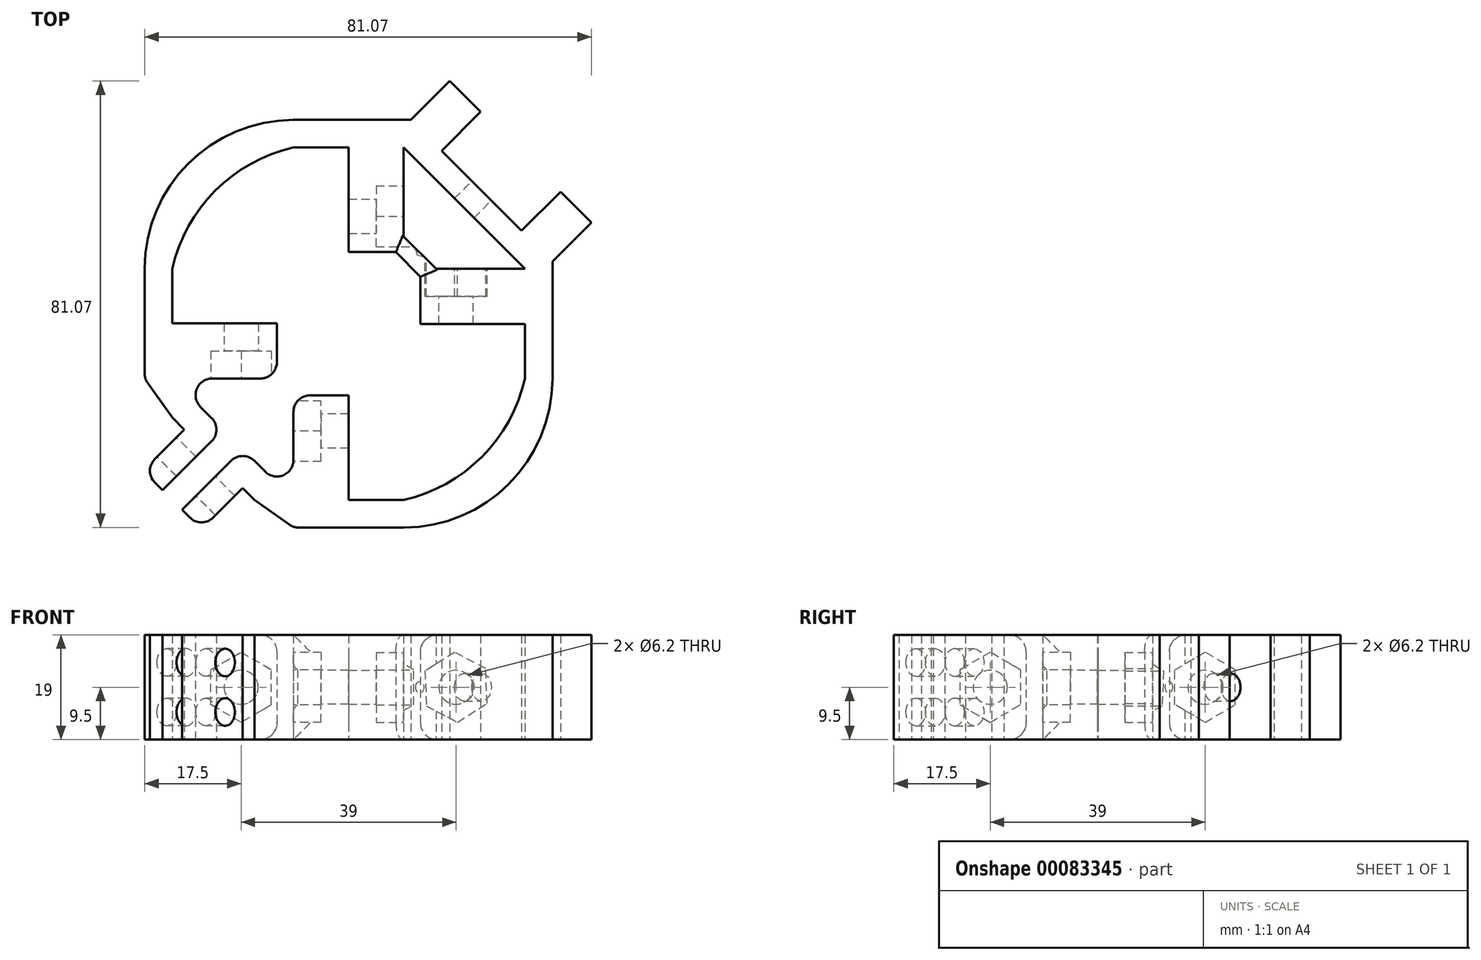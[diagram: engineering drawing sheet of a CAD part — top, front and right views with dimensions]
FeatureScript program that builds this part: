
annotation { "Feature Type Name" : "Feature", "Feature Type Description" : "" }
export const myFeature = defineFeature(function(context is Context, id is Id, definition is map)
    precondition{}
    {
        {
            var Q0;
            Q0=qCreatedBy(makeId("Top.planeOp"),FACE);
            var sketch = newSketch(context, id + "F0", { "sketchPlane" : qUnion([Q0])});
            skLineSegment(sketch, "E0.bottom", {"start": v(-10, 10) * mm, "end": v(10, 10) * mm, "construction": true});
            skLineSegment(sketch, "E0.top", {"start": v(-10, -10) * mm, "end": v(10, -10) * mm, "construction": true});
            skLineSegment(sketch, "E0.left", {"start": v(-10, 10) * mm, "end": v(-10, -10) * mm, "construction": true});
            skLineSegment(sketch, "E0.right", {"start": v(10, 10) * mm, "end": v(10, -10) * mm, "construction": true});
            skPoint(sketch, "E0.middle", {"position": v(0, 0) * mm});
            skLineSegment(sketch, "E1.0", {"start": v(-19.5, 19.5) * mm, "end": v(19.5, 19.5) * mm, "construction": true});
            skLineSegment(sketch, "E1.1", {"start": v(-19.5, 19.5) * mm, "end": v(-19.5, -19.5) * mm, "construction": true});
            skLineSegment(sketch, "E1.2", {"start": v(-19.5, -19.5) * mm, "end": v(19.5, -19.5) * mm, "construction": true});
            skLineSegment(sketch, "E1.3", {"start": v(19.5, 19.5) * mm, "end": v(19.5, -19.5) * mm, "construction": true});
            skLineSegment(sketch, "E2.0", {"start": v(-29, 29) * mm, "end": v(29, 29) * mm, "construction": true});
            skLineSegment(sketch, "E2.1", {"start": v(-29, 29) * mm, "end": v(-29, -29) * mm, "construction": true});
            skLineSegment(sketch, "E2.2", {"start": v(-29, -29) * mm, "end": v(29, -29) * mm, "construction": true});
            skLineSegment(sketch, "E2.3", {"start": v(29, 29) * mm, "end": v(29, -29) * mm, "construction": true});
            skLineSegment(sketch, "E3", {"start": v(0, 10) * mm, "end": v(0, 29) * mm});
            skLineSegment(sketch, "E4", {"start": v(10, 0) * mm, "end": v(29, 0) * mm, "construction": true});
            skLineSegment(sketch, "E5", {"start": v(0, -10) * mm, "end": v(0, -29) * mm, "construction": true});
            skLineSegment(sketch, "E6", {"start": v(-10, 0) * mm, "end": v(-29, 0) * mm, "construction": true});
            skLineSegment(sketch, "E7.0", {"start": v(-10, 3) * mm, "end": v(-29, 3) * mm, "construction": true});
            skLineSegment(sketch, "E8.0", {"start": v(10, -3) * mm, "end": v(29, -3) * mm, "construction": true});
            skLineSegment(sketch, "E9.0", {"start": v(-10, -3) * mm, "end": v(-29, -3) * mm, "construction": true});
            skLineSegment(sketch, "E10.0", {"start": v(10, 3) * mm, "end": v(29, 3) * mm, "construction": true});
            skLineSegment(sketch, "E11.0", {"start": v(3, 10) * mm, "end": v(3, 29) * mm, "construction": true});
            skLineSegment(sketch, "E12.0", {"start": v(-3, 10) * mm, "end": v(-3, 29) * mm, "construction": true});
            skLineSegment(sketch, "E13.0", {"start": v(-3, -10) * mm, "end": v(-3, -29) * mm, "construction": true});
            skLineSegment(sketch, "E14.0", {"start": v(3, -10) * mm, "end": v(3, -29) * mm, "construction": true});
            skLineSegment(sketch, "E15.0", {"start": v(-32, 32) * mm, "end": v(-32, -32) * mm});
            skLineSegment(sketch, "E15.1", {"start": v(-32, 32) * mm, "end": v(32, 32) * mm});
            skLineSegment(sketch, "E15.2", {"start": v(32, 32) * mm, "end": v(32, -32) * mm});
            skLineSegment(sketch, "E15.3", {"start": v(-32, -32) * mm, "end": v(32, -32) * mm});
            skLineSegment(sketch, "E16.0", {"start": v(-37, 37) * mm, "end": v(37, 37) * mm});
            skLineSegment(sketch, "E16.1", {"start": v(-37, 37) * mm, "end": v(-37, -37) * mm});
            skLineSegment(sketch, "E16.2", {"start": v(-37, -37) * mm, "end": v(37, -37) * mm});
            skLineSegment(sketch, "E16.3", {"start": v(37, 37) * mm, "end": v(37, -37) * mm});
            skLineSegment(sketch, "E17.MirrorCS", {"start": v(0, 13) * mm, "end": v(-10, 13) * mm, "construction": true});
            skLineSegment(sketch, "E18.MirrorCS", {"start": v(-10, 13) * mm, "end": v(-10, 32) * mm, "construction": true});
            skLineSegment(sketch, "E19.MirrorCS", {"start": v(0, 32) * mm, "end": v(0, 13) * mm, "construction": true});
            skLineSegment(sketch, "E20.MirrorCS", {"start": v(10, -13) * mm, "end": v(10, -32) * mm});
            skLineSegment(sketch, "E21.MirrorCS", {"start": v(0, -32) * mm, "end": v(0, -13) * mm});
            skLineSegment(sketch, "E22.MirrorCS", {"start": v(0, -13) * mm, "end": v(10, -13) * mm});
            skLineSegment(sketch, "E23.MirrorCS", {"start": v(32, 0.05) * mm, "end": v(13.05, 0.05) * mm, "construction": true});
            skLineSegment(sketch, "E24.MirrorCS", {"start": v(13.05, -9.95) * mm, "end": v(32, -9.95) * mm, "construction": true});
            skLineSegment(sketch, "E25.MirrorCS", {"start": v(13.05, 0.05) * mm, "end": v(13.05, -9.95) * mm, "construction": true});
            skLineSegment(sketch, "E26.MirrorCS", {"start": v(-32, -0.05) * mm, "end": v(-13, -0.05) * mm});
            skLineSegment(sketch, "E27.MirrorCS", {"start": v(-13, 9.95) * mm, "end": v(-32, 9.95) * mm});
            skLineSegment(sketch, "E28.MirrorCS", {"start": v(-13, -0.05) * mm, "end": v(-13, 9.95) * mm});
            skLineSegment(sketch, "E29", {"start": v(16.28, 32) * mm, "end": v(32, 16.28) * mm});
            skLineSegment(sketch, "E30", {"start": v(16.28, 32) * mm, "end": v(11.28, 37) * mm});
            skLineSegment(sketch, "E31", {"start": v(32, 16.28) * mm, "end": v(37, 11.28) * mm});
            skLineSegment(sketch, "E32", {"start": v(10, 32) * mm, "end": v(32, 9.95) * mm});
            skArc(sketch, "E33", {"start": v(-10, 32) * mm, "mid": v(-25.56, 25.56) * mm, "end": v(-32, 10) * mm});
            skArc(sketch, "E34", {"start": v(-10, 37) * mm, "mid": v(-29.1, 29.1) * mm, "end": v(-37, 10) * mm});
            skArc(sketch, "E35", {"start": v(10, -32) * mm, "mid": v(25.56, -25.56) * mm, "end": v(32, -10) * mm});
            skArc(sketch, "E36", {"start": v(10, -37) * mm, "mid": v(29.1, -29.1) * mm, "end": v(37, -10) * mm});
            skLineSegment(sketch, "E37.MirrorCS", {"start": v(13.05, -0.05) * mm, "end": v(13.05, 9.95) * mm});
            skLineSegment(sketch, "E38.MirrorCS", {"start": v(32, -0.05) * mm, "end": v(13.05, -0.05) * mm});
            skLineSegment(sketch, "E39.MirrorCS", {"start": v(13.05, 9.95) * mm, "end": v(32, 9.95) * mm});
            skLineSegment(sketch, "E40.MirrorCS", {"start": v(-10, -13) * mm, "end": v(-10, -32) * mm});
            skLineSegment(sketch, "E41.MirrorCS", {"start": v(0, -13) * mm, "end": v(-10, -13) * mm});
            skLineSegment(sketch, "E42.MirrorCS", {"start": v(-13, -9.95) * mm, "end": v(-32, -9.95) * mm});
            skLineSegment(sketch, "E43.MirrorCS", {"start": v(-32, 0.05) * mm, "end": v(-13, 0.05) * mm});
            skLineSegment(sketch, "E44.MirrorCS", {"start": v(-13, 0.05) * mm, "end": v(-13, -9.95) * mm});
            skLineSegment(sketch, "E45.MirrorCS", {"start": v(0, 13) * mm, "end": v(10, 13) * mm});
            skLineSegment(sketch, "E46.MirrorCS", {"start": v(0, 32) * mm, "end": v(0, 13) * mm});
            skLineSegment(sketch, "E47.MirrorCS", {"start": v(10, 13) * mm, "end": v(10, 32) * mm});
            skLineSegment(sketch, "E48", {"start": v(10, 13) * mm, "end": v(13.05, 9.95) * mm});
            skLineSegment(sketch, "E49", {"start": v(-32, -9.95) * mm, "end": v(-37, -10) * mm});
            skLineSegment(sketch, "E50", {"start": v(-10, -32) * mm, "end": v(-10, -37) * mm});
            skLineSegment(sketch, "E51", {"start": v(10, 15.83) * mm, "end": v(15.88, 9.95) * mm});
            skLineSegment(sketch, "E52", {"start": v(8.59, 13) * mm, "end": v(13.05, 8.54) * mm});
            skLineSegment(sketch, "E53", {"start": v(-32, -9.95) * mm, "end": v(-10, -32) * mm});
            skLineSegment(sketch, "E54.0", {"start": v(-35.54, -13.48) * mm, "end": v(-13.54, -35.53) * mm, "construction": true});
            skLineSegment(sketch, "E55", {"start": v(-32, -17.03) * mm, "end": v(-17.06, -32) * mm});
            skLineSegment(sketch, "E56", {"start": v(-32, -32) * mm, "end": v(-20.98, -21) * mm, "construction": true});
            skLineSegment(sketch, "E57.0", {"start": v(-30.94, -33.06) * mm, "end": v(-19.92, -22.06) * mm, "construction": true});
            skLineSegment(sketch, "E58.0", {"start": v(-33.06, -30.94) * mm, "end": v(-22.04, -19.94) * mm, "construction": true});
            skLineSegment(sketch, "E59", {"start": v(-22.04, -19.94) * mm, "end": v(-25.57, -23.47) * mm});
            skLineSegment(sketch, "E60", {"start": v(-23.46, -25.6) * mm, "end": v(-19.92, -22.06) * mm});
            skLineSegment(sketch, "E61", {"start": v(-25.57, -23.47) * mm, "end": v(-29, -26.89) * mm});
            skLineSegment(sketch, "E62", {"start": v(-29, -26.89) * mm, "end": v(-33.24, -22.64) * mm});
            skLineSegment(sketch, "E63", {"start": v(-33.24, -22.64) * mm, "end": v(-29.81, -19.22) * mm});
            skLineSegment(sketch, "E64", {"start": v(-23.46, -25.6) * mm, "end": v(-26.87, -29) * mm});
            skLineSegment(sketch, "E65", {"start": v(-26.87, -29) * mm, "end": v(-22.63, -33.25) * mm});
            skLineSegment(sketch, "E66", {"start": v(-22.63, -33.25) * mm, "end": v(-19.22, -29.84) * mm});
            skLineSegment(sketch, "E67", {"start": v(-32, -17.03) * mm, "end": v(-37, -10) * mm});
            skLineSegment(sketch, "E68", {"start": v(-17.06, -32) * mm, "end": v(-10, -37) * mm});
            skLineSegment(sketch, "E69", {"start": v(-26.87, -29) * mm, "end": v(-30.94, -33.06) * mm});
            skLineSegment(sketch, "E70", {"start": v(-30.94, -33.06) * mm, "end": v(-26.7, -37.3) * mm});
            skLineSegment(sketch, "E71", {"start": v(-26.7, -37.3) * mm, "end": v(-22.63, -33.25) * mm});
            skLineSegment(sketch, "E72", {"start": v(-29, -26.89) * mm, "end": v(-33.06, -30.94) * mm});
            skLineSegment(sketch, "E73", {"start": v(-33.06, -30.94) * mm, "end": v(-37.3, -26.7) * mm});
            skLineSegment(sketch, "E74", {"start": v(-37.3, -26.7) * mm, "end": v(-33.24, -22.64) * mm});
            skLineSegment(sketch, "E75.0", {"start": v(-29.7, -26.18) * mm, "end": v(-33.77, -30.23) * mm});
            skLineSegment(sketch, "E75.1", {"start": v(-26.28, -22.76) * mm, "end": v(-29.7, -26.18) * mm});
            skLineSegment(sketch, "E75.2", {"start": v(-22.74, -19.23) * mm, "end": v(-26.28, -22.76) * mm});
            skLineSegment(sketch, "E76.0", {"start": v(-22.75, -26.3) * mm, "end": v(-19.2, -22.77) * mm});
            skLineSegment(sketch, "E76.1", {"start": v(-22.75, -26.3) * mm, "end": v(-26.16, -29.7) * mm});
            skLineSegment(sketch, "E76.2", {"start": v(-26.16, -29.7) * mm, "end": v(-30.23, -33.77) * mm});
            skArc(sketch, "E77", {"start": v(-10, 32) * mm, "mid": v(-24.18, 24.18) * mm, "end": v(-32, 10) * mm});
            skArc(sketch, "E78", {"start": v(10, -32) * mm, "mid": v(24.19, -24.16) * mm, "end": v(32, -9.95) * mm});
            skSolve(sketch);
        }
        {
            var Q0;
            {var subQ0=sQuery(id+"F0.wireOp",EDGE,"E29");Q0=makeQuery(id+"F0.imprint","IMPRINT",FACE,{"disambiguationData":[TD([[makeQuery(id+"F0.imprint","IMPRINT",EDGE,{"derivedFrom":subQ0}),-1.0]])]});}
            var Q1;
            {var subQ0=sQuery(id+"F0.wireOp",EDGE,"E30");Q1=makeQuery(id+"F0.imprint","IMPRINT",FACE,{"disambiguationData":[TD([[makeQuery(id+"F0.imprint","IMPRINT",EDGE,{"derivedFrom":subQ0}),1.0]])]});}
            var Q2;
            {var subQ6=sQuery(id+"F0.wireOp",EDGE,"E31");Q2=makeQuery(id+"F0.imprint","IMPRINT",FACE,{"disambiguationData":[TD([[makeQuery(id+"F0.imprint","IMPRINT",EDGE,{"derivedFrom":subQ6}),-1.0]])]});}
            var Q3;
            Q3=makeQuery(id+"F0.imprint","IMPRINT",FACE,{"disambiguationData":[TD([[makeQuery(id+"F0.imprint","IMPRINT",EDGE,{"derivedFrom":sQuery(id+"F0.wireOp",EDGE,"E37.MirrorCS")}),-1.0]])]});
            var Q4;
            Q4=makeQuery(id+"F0.imprint","IMPRINT",FACE,{"disambiguationData":[TD([[makeQuery(id+"F0.imprint","IMPRINT",EDGE,{"derivedFrom":sQuery(id+"F0.wireOp",EDGE,"E45.MirrorCS")}),1.0]])]});
            var Q5;
            {var subQ0=sQuery(id+"F0.wireOp",EDGE,"E26.MirrorCS");Q5=makeQuery(id+"F0.imprint","IMPRINT",FACE,{"disambiguationData":[TD([[makeQuery(id+"F0.imprint","IMPRINT",EDGE,{"derivedFrom":subQ0}),1.0]])]});}
            var Q6;
            {var subQ8=sQuery(id+"F0.wireOp",EDGE,"E50");Q6=makeQuery(id+"F0.imprint","IMPRINT",FACE,{"disambiguationData":[TD([[makeQuery(id+"F0.imprint","IMPRINT",EDGE,{"derivedFrom":subQ8}),1.0]])]});}
            var Q7;
            {var subQ0=sQuery(id+"F0.wireOp",EDGE,"E35");Q7=makeQuery(id+"F0.imprint","IMPRINT",FACE,{"disambiguationData":[TD([[makeQuery(id+"F0.imprint","IMPRINT",EDGE,{"derivedFrom":subQ0}),-1.0]])]});}
            var Q8;
            {var subQ0=sQuery(id+"F0.wireOp",EDGE,"E49");Q8=makeQuery(id+"F0.imprint","IMPRINT",FACE,{"disambiguationData":[TD([[makeQuery(id+"F0.imprint","IMPRINT",EDGE,{"derivedFrom":subQ0}),-1.0]])]});}
            var Q9;
            {var subQ0=sQuery(id+"F0.wireOp",EDGE,"E33");Q9=makeQuery(id+"F0.imprint","IMPRINT",FACE,{"disambiguationData":[TD([[makeQuery(id+"F0.imprint","IMPRINT",EDGE,{"derivedFrom":subQ0}),-1.0]])]});}
            var Q10;
            {var subQ0=sQuery(id+"F0.wireOp",EDGE,"E48");Q10=makeQuery(id+"F0.imprint","IMPRINT",FACE,{"disambiguationData":[TD([[makeQuery(id+"F0.imprint","IMPRINT",EDGE,{"derivedFrom":subQ0}),1.0]])]});}
            var Q11;
            {var subQ0=sQuery(id+"F0.wireOp",EDGE,"E48");Q11=makeQuery(id+"F0.imprint","IMPRINT",FACE,{"disambiguationData":[TD([[makeQuery(id+"F0.imprint","IMPRINT",EDGE,{"derivedFrom":subQ0}),-1.0]])]});}
            var Q12;
            {var subQ0=sQuery(id+"F0.wireOp",EDGE,"E49");Q12=makeQuery(id+"F0.imprint","IMPRINT",FACE,{"disambiguationData":[TD([[makeQuery(id+"F0.imprint","IMPRINT",EDGE,{"derivedFrom":subQ0}),1.0]])]});}
            var Q13;
            {var subQ0=sQuery(id+"F0.wireOp",EDGE,"E50");Q13=makeQuery(id+"F0.imprint","IMPRINT",FACE,{"disambiguationData":[TD([[makeQuery(id+"F0.imprint","IMPRINT",EDGE,{"derivedFrom":subQ0}),-1.0]])]});}
            var Q14;
            {var subQ0=sQuery(id+"F0.wireOp",EDGE,"E62");var subQ1=sQuery(id+"F0.wireOp",EDGE,"E15.0");var subQ2=makeQuery(id+"F0.imprint","INTERSECT",VERTEX,{"derivedFrom":[subQ1,subQ0]});Q14=makeQuery(id+"F0.imprint","IMPRINT",FACE,{"disambiguationData":[TD([[makeQuery(id+"F0.imprint","IMPRINT",EDGE,{"disambiguationData":[TD([[subQ2,-1.0]])],"derivedFrom":subQ1}),1.0]])]});}
            var Q15;
            {var subQ0=sQuery(id+"F0.wireOp",EDGE,"E73");Q15=makeQuery(id+"F0.imprint","IMPRINT",FACE,{"disambiguationData":[TD([[makeQuery(id+"F0.imprint","IMPRINT",EDGE,{"derivedFrom":subQ0}),-1.0]])]});}
            var Q16;
            {var subQ0=sQuery(id+"F0.wireOp",EDGE,"E70");Q16=makeQuery(id+"F0.imprint","IMPRINT",FACE,{"disambiguationData":[TD([[makeQuery(id+"F0.imprint","IMPRINT",EDGE,{"derivedFrom":subQ0}),1.0]])]});}
            var Q17;
            {var subQ0=sQuery(id+"F0.wireOp",EDGE,"E65");var subQ1=sQuery(id+"F0.wireOp",EDGE,"E15.3");var subQ2=makeQuery(id+"F0.imprint","INTERSECT",VERTEX,{"derivedFrom":[subQ1,subQ0]});Q17=makeQuery(id+"F0.imprint","IMPRINT",FACE,{"disambiguationData":[TD([[makeQuery(id+"F0.imprint","IMPRINT",EDGE,{"disambiguationData":[TD([[subQ2,-1.0]])],"derivedFrom":subQ1}),-1.0]])]});}
            var Q18;
            {var subQ0=sQuery(id+"F0.wireOp",EDGE,"E63");var subQ1=sQuery(id+"F0.wireOp",EDGE,"E15.0");var subQ2=makeQuery(id+"F0.imprint","INTERSECT",VERTEX,{"derivedFrom":[subQ1,subQ0]});Q18=makeQuery(id+"F0.imprint","IMPRINT",FACE,{"disambiguationData":[TD([[makeQuery(id+"F0.imprint","IMPRINT",EDGE,{"disambiguationData":[TD([[subQ2,-1.0]])],"derivedFrom":subQ1}),-1.0]])]});}
            var Q19;
            {var subQ0=sQuery(id+"F0.wireOp",EDGE,"E21.MirrorCS");Q19=makeQuery(id+"F0.imprint","IMPRINT",FACE,{"disambiguationData":[TD([[makeQuery(id+"F0.imprint","IMPRINT",EDGE,{"derivedFrom":subQ0}),1.0]])]});}
            var Q20;
            {var subQ0=sQuery(id+"F0.wireOp",EDGE,"E26.MirrorCS");Q20=makeQuery(id+"F0.imprint","IMPRINT",FACE,{"disambiguationData":[TD([[makeQuery(id+"F0.imprint","IMPRINT",EDGE,{"derivedFrom":subQ0}),-1.0]])]});}
            var Q21;
            {var subQ3=sQuery(id+"F0.wireOp",EDGE,"E15.0");var subQ6=sQuery(id+"F0.wireOp",EDGE,"E62");var subQ10=makeQuery(id+"F0.imprint","INTERSECT",VERTEX,{"derivedFrom":[subQ3,subQ6]});Q21=makeQuery(id+"F0.imprint","IMPRINT",FACE,{"disambiguationData":[TD([[makeQuery(id+"F0.imprint","IMPRINT",EDGE,{"disambiguationData":[TD([[subQ10,-1.0]])],"derivedFrom":subQ3}),-1.0]])]});}
            var Q22;
            {var subQ6=sQuery(id+"F0.wireOp",EDGE,"E75.2");Q22=makeQuery(id+"F0.imprint","IMPRINT",FACE,{"disambiguationData":[TD([[makeQuery(id+"F0.imprint","IMPRINT",EDGE,{"derivedFrom":subQ6}),-1.0]])]});}
            var Q23;
            {var subQ5=sQuery(id+"F0.wireOp",EDGE,"E75.1");Q23=makeQuery(id+"F0.imprint","IMPRINT",FACE,{"disambiguationData":[TD([[makeQuery(id+"F0.imprint","IMPRINT",EDGE,{"derivedFrom":subQ5}),-1.0]])]});}
            var Q24;
            {var subQ6=sQuery(id+"F0.wireOp",EDGE,"E76.0");Q24=makeQuery(id+"F0.imprint","IMPRINT",FACE,{"disambiguationData":[TD([[makeQuery(id+"F0.imprint","IMPRINT",EDGE,{"derivedFrom":subQ6}),-1.0]])]});}
            var Q25;
            {var subQ0=sQuery(id+"F0.wireOp",EDGE,"E76.1");Q25=makeQuery(id+"F0.imprint","IMPRINT",FACE,{"disambiguationData":[TD([[makeQuery(id+"F0.imprint","IMPRINT",EDGE,{"derivedFrom":subQ0}),1.0]])]});}
            var Q26;
            {var subQ0=sQuery(id+"F0.wireOp",EDGE,"E76.2");var subQ8=sQuery(id+"F0.wireOp",EDGE,"E15.3");var subQ11=makeQuery(id+"F0.imprint","INTERSECT",VERTEX,{"derivedFrom":[subQ8,subQ0]});Q26=makeQuery(id+"F0.imprint","IMPRINT",FACE,{"disambiguationData":[TD([[makeQuery(id+"F0.imprint","IMPRINT",EDGE,{"disambiguationData":[TD([[subQ11,-1.0]])],"derivedFrom":subQ8}),-1.0]])]});}
            var Q27;
            {var subQ0=sQuery(id+"F0.wireOp",EDGE,"E76.2");var subQ1=sQuery(id+"F0.wireOp",EDGE,"E15.3");var subQ2=makeQuery(id+"F0.imprint","INTERSECT",VERTEX,{"derivedFrom":[subQ1,subQ0]});Q27=makeQuery(id+"F0.imprint","IMPRINT",FACE,{"disambiguationData":[TD([[makeQuery(id+"F0.imprint","IMPRINT",EDGE,{"disambiguationData":[TD([[subQ2,-1.0]])],"derivedFrom":subQ1}),1.0]])]});}
            var Q28;
            Q28=makeQuery(id+"F0.imprint","IMPRINT",FACE,{"disambiguationData":[TD([[makeQuery(id+"F0.imprint","IMPRINT",EDGE,{"derivedFrom":sQuery(id+"F0.wireOp",EDGE,"E33")}),1.0]])]});
            var Q29;
            {var subQ0=sQuery(id+"F0.wireOp",EDGE,"E35");Q29=makeQuery(id+"F0.imprint","IMPRINT",FACE,{"disambiguationData":[TD([[makeQuery(id+"F0.imprint","IMPRINT",EDGE,{"derivedFrom":subQ0}),1.0]])]});}
            extrude(context, id + "F1", {"entities" : qUnion([Q0, Q1, Q2, Q3, Q4, Q5, Q6, Q7, Q8, Q9, Q10, Q11, Q12, Q13, Q14, Q15, Q16, Q17, Q18, Q19, Q20, Q21, Q22, Q23, Q24, Q25, Q26, Q27, Q28, Q29]), "depth" : 19 * mm});
        }
        {
            var Q0;
            Q0=makeQuery(id+"F1.opExtrude","SWEPT_FACE",FACE,{"disambiguationData":[OSD([sQuery(id+"F0.wireOp",EDGE,"E40.MirrorCS")])]});
            var sketch = newSketch(context, id + "F2", { "sketchPlane" : qUnion([Q0])});
            skLineSegment(sketch, "E79", {"start": v(19.5, 9.5) * mm, "end": v(32, 9.5) * mm, "construction": true});
            skCircle(sketch, "E80.cCircle", {"center": v(19.5, 9.5) * mm, "radius": 5.5 * mm, "construction": true});
            skLineSegment(sketch, "E80.0", {"start": v(14, 6.32) * mm, "end": v(14, 12.68) * mm});
            skLineSegment(sketch, "E80.1", {"start": v(14, 12.68) * mm, "end": v(19.5, 15.85) * mm});
            skLineSegment(sketch, "E80.2", {"start": v(19.5, 15.85) * mm, "end": v(25, 12.68) * mm});
            skLineSegment(sketch, "E80.3", {"start": v(25, 12.68) * mm, "end": v(25, 6.32) * mm});
            skLineSegment(sketch, "E80.4", {"start": v(25, 6.32) * mm, "end": v(19.5, 3.15) * mm});
            skLineSegment(sketch, "E80.5", {"start": v(19.5, 3.15) * mm, "end": v(14, 6.32) * mm});
            skPoint(sketch, "E80.0.midPoint", {"position": v(14, 9.5) * mm});
            skSolve(sketch);
        }
        {
            var Q0;
            Q0=makeQuery(id+"F2.imprint","IMPRINT",FACE,{"disambiguationData":[TD([[makeQuery(id+"F2.imprint","IMPRINT",EDGE,{"derivedFrom":sQuery(id+"F2.wireOp",EDGE,"b893e4e9-6a1b-4cab-829b-d1a7efe0a6880.MirrorCS")}),1.0]])]});
            var Q1;
            Q1=makeQuery(id+"F2.imprint","IMPRINT",FACE,{"disambiguationData":[TD([[makeQuery(id+"F2.imprint","IMPRINT",EDGE,{"derivedFrom":sQuery(id+"F2.wireOp",EDGE,"E80.0")}),-1.0]])]});
            extrude(context, id + "F3", {"entities" : qUnion([Q0, Q1]), "operationType" : NewBodyOperationType.REMOVE, "oppositeDirection" : true, "depth" : 5 * mm});
        }
        {
            var Q0;
            Q0=makeQuery(id+"F1.opExtrude","SWEPT_FACE",FACE,{"disambiguationData":[OSD([sQuery(id+"F0.wireOp",EDGE,"E42.MirrorCS")])]});
            var sketch = newSketch(context, id + "F4", { "sketchPlane" : qUnion([Q0])});
            skLineSegment(sketch, "E81", {"start": v(-32, 9.5) * mm, "end": v(-19.5, 9.5) * mm, "construction": true});
            skPoint(sketch, "E81.endSnap0", {"position": v(-32, 9.5) * mm});
            skCircle(sketch, "E82.cCircle", {"center": v(-19.5, 9.5) * mm, "radius": 5.5 * mm, "construction": true});
            skLineSegment(sketch, "E82.0", {"start": v(-14, 12.68) * mm, "end": v(-14, 6.32) * mm});
            skLineSegment(sketch, "E82.1", {"start": v(-14, 6.32) * mm, "end": v(-19.5, 3.15) * mm});
            skLineSegment(sketch, "E82.2", {"start": v(-19.5, 3.15) * mm, "end": v(-25, 6.32) * mm});
            skLineSegment(sketch, "E82.3", {"start": v(-25, 6.32) * mm, "end": v(-25, 12.68) * mm});
            skLineSegment(sketch, "E82.4", {"start": v(-25, 12.68) * mm, "end": v(-19.5, 15.85) * mm});
            skLineSegment(sketch, "E82.5", {"start": v(-19.5, 15.85) * mm, "end": v(-14, 12.68) * mm});
            skPoint(sketch, "E82.0.midPoint", {"position": v(-14, 9.5) * mm});
            skSolve(sketch);
        }
        {
            var Q0;
            Q0=makeQuery(id+"F4.imprint","IMPRINT",FACE,{"disambiguationData":[TD([[makeQuery(id+"F4.imprint","IMPRINT",EDGE,{"derivedFrom":sQuery(id+"F4.wireOp",EDGE,"E82.0")}),-1.0]])]});
            extrude(context, id + "F5", {"entities" : qUnion([Q0]), "operationType" : NewBodyOperationType.REMOVE, "oppositeDirection" : true, "depth" : 5 * mm});
        }
        {
            var Q0;
            Q0=makeQuery(id+"F1.opExtrude","SWEPT_FACE",FACE,{"disambiguationData":[OSD([sQuery(id+"F0.wireOp",EDGE,"E47.MirrorCS")])]});
            var sketch = newSketch(context, id + "F6", { "sketchPlane" : qUnion([Q0])});
            skSolve(sketch);
        }
        {
            var Q0;
            Q0=makeQuery(id+"F1.opExtrude","SWEPT_FACE",FACE,{"disambiguationData":[OSD([sQuery(id+"F0.wireOp",EDGE,"E39.MirrorCS")])]});
            var sketch = newSketch(context, id + "F7", { "sketchPlane" : qUnion([Q0])});
            skLineSegment(sketch, "E83", {"start": v(-32, 9.5) * mm, "end": v(-19.5, 9.5) * mm, "construction": true});
            skCircle(sketch, "E84.cCircle", {"center": v(-19.5, 9.5) * mm, "radius": 5.5 * mm, "construction": true});
            skLineSegment(sketch, "E84.0", {"start": v(-13.87, 12.45) * mm, "end": v(-14.13, 6.1) * mm});
            skLineSegment(sketch, "E84.1", {"start": v(-14.13, 6.1) * mm, "end": v(-19.76, 3.15) * mm});
            skLineSegment(sketch, "E84.2", {"start": v(-19.76, 3.15) * mm, "end": v(-25.13, 6.55) * mm});
            skLineSegment(sketch, "E84.3", {"start": v(-25.13, 6.55) * mm, "end": v(-24.87, 12.9) * mm});
            skLineSegment(sketch, "E84.4", {"start": v(-24.87, 12.9) * mm, "end": v(-19.24, 15.85) * mm});
            skLineSegment(sketch, "E84.5", {"start": v(-19.24, 15.85) * mm, "end": v(-13.87, 12.45) * mm});
            skPoint(sketch, "E84.0.midPoint", {"position": v(-14, 9.27) * mm});
            skSolve(sketch);
        }
        {
            var Q0;
            Q0=makeQuery(id+"F7.imprint","IMPRINT",FACE,{"disambiguationData":[TD([[makeQuery(id+"F7.imprint","IMPRINT",EDGE,{"derivedFrom":sQuery(id+"F7.wireOp",EDGE,"E84.0")}),-1.0]])]});
            var Q1;
            {var subQ1=sQuery(id+"F7.wireOp",EDGE,"E84.2");Q1=makeQuery(id+"F7.imprint","IMPRINT",FACE,{"disambiguationData":[TD([[makeQuery(id+"F7.imprint","IMPRINT",EDGE,{"derivedFrom":subQ1}),-1.0]])]});}
            extrude(context, id + "F8", {"entities" : qUnion([Q0, Q1]), "operationType" : NewBodyOperationType.REMOVE, "endBound" : BoundingType.SYMMETRIC, "oppositeDirection" : true, "depth" : 10 * mm});
        }
        {
            var Q0;
            {var subQ0=sQuery(id+"F0.wireOp",EDGE,"E47.MirrorCS");Q0=makeQuery(id+"F6.imprint","IMPRINT",FACE,{"disambiguationData":[TD([[makeQuery(id+"F6.imprint","IMPRINT",EDGE,{"derivedFrom":makeQuery(id+"F1.opExtrude","CAP_EDGE",EDGE,{"disambiguationData":[OSD([subQ0])],"isStart":true})}),1.0]])]});}
            var sketch = newSketch(context, id + "F9", { "sketchPlane" : qUnion([Q0])});
            skLineSegment(sketch, "E85.0", {"start": v(19.5, 22) * mm, "end": v(19.5, -3) * mm, "construction": true});
            skCircle(sketch, "E86.cCircle", {"center": v(19.5, 9.5) * mm, "radius": 5.5 * mm, "construction": true});
            skLineSegment(sketch, "E86.0", {"start": v(14, 6.32) * mm, "end": v(14, 12.68) * mm});
            skLineSegment(sketch, "E86.1", {"start": v(14, 12.68) * mm, "end": v(19.5, 15.85) * mm});
            skLineSegment(sketch, "E86.2", {"start": v(19.5, 15.85) * mm, "end": v(25, 12.68) * mm});
            skLineSegment(sketch, "E86.3", {"start": v(25, 12.68) * mm, "end": v(25, 6.32) * mm});
            skLineSegment(sketch, "E86.4", {"start": v(25, 6.32) * mm, "end": v(19.5, 3.15) * mm});
            skLineSegment(sketch, "E86.5", {"start": v(19.5, 3.15) * mm, "end": v(14, 6.32) * mm});
            skPoint(sketch, "E86.0.midPoint", {"position": v(14, 9.5) * mm});
            skSolve(sketch);
        }
        {
            var Q0;
            Q0=sQuery(id+"F2.wireOp",VERTEX,"E79.start");
            var Q1;
            Q1=sQuery(id+"F4.wireOp",VERTEX,"E81.end");
            var Q2;
            Q2=sQuery(id+"F9.wireOp",VERTEX,"E86.cCircle.center");
            var Q3;
            Q3=sQuery(id+"F7.wireOp",VERTEX,"E83.end");
            var Q4;
            Q4=makeQuery(id+"F1.opExtrude","SWEPT_BODY",BODY,{"disambiguationData":[OSD([sQuery(id+"F0.wireOp",EDGE,"E15.0"),sQuery(id+"F0.wireOp",EDGE,"E15.1"),sQuery(id+"F0.wireOp",EDGE,"E15.2"),sQuery(id+"F0.wireOp",EDGE,"E15.3"),sQuery(id+"F0.wireOp",EDGE,"E16.0"),sQuery(id+"F0.wireOp",EDGE,"E16.1"),sQuery(id+"F0.wireOp",EDGE,"E16.2"),sQuery(id+"F0.wireOp",EDGE,"E16.3"),sQuery(id+"F0.wireOp",EDGE,"E20.MirrorCS"),sQuery(id+"F0.wireOp",EDGE,"E21.MirrorCS"),sQuery(id+"F0.wireOp",EDGE,"E22.MirrorCS"),sQuery(id+"F0.wireOp",EDGE,"E26.MirrorCS"),sQuery(id+"F0.wireOp",EDGE,"E27.MirrorCS"),sQuery(id+"F0.wireOp",EDGE,"E28.MirrorCS"),sQuery(id+"F0.wireOp",EDGE,"E29"),sQuery(id+"F0.wireOp",EDGE,"E30"),sQuery(id+"F0.wireOp",EDGE,"E31"),sQuery(id+"F0.wireOp",EDGE,"E32"),sQuery(id+"F0.wireOp",EDGE,"E33"),sQuery(id+"F0.wireOp",EDGE,"E34"),sQuery(id+"F0.wireOp",EDGE,"E35"),sQuery(id+"F0.wireOp",EDGE,"E36"),sQuery(id+"F0.wireOp",EDGE,"E37.MirrorCS"),sQuery(id+"F0.wireOp",EDGE,"E38.MirrorCS"),sQuery(id+"F0.wireOp",EDGE,"E39.MirrorCS"),sQuery(id+"F0.wireOp",EDGE,"E45.MirrorCS"),sQuery(id+"F0.wireOp",EDGE,"E46.MirrorCS"),sQuery(id+"F0.wireOp",EDGE,"E47.MirrorCS"),sQuery(id+"F0.wireOp",EDGE,"E49"),sQuery(id+"F0.wireOp",EDGE,"E50")])]});
            hole(context, id + "F10", {"style" : HoleStyle.SIMPLE, "endStyle" : HoleEndStyle.BLIND, "holeDiameter" : 6.2 * mm, "holeDepth" : 10 * mm, "locations" : qUnion([Q0, Q1, Q2, Q3]), "scope" : qUnion([Q4])});
        }
        {
            var Q0;
            Q0=makeQuery(id+"F9.imprint","IMPRINT",FACE,{"disambiguationData":[TD([[makeQuery(id+"F9.imprint","IMPRINT",EDGE,{"derivedFrom":sQuery(id+"F9.wireOp",EDGE,"E86.0")}),-1.0]])]});
            var Q1;
            {var subQ1=sQuery(id+"F9.wireOp",EDGE,"E86.2");Q1=makeQuery(id+"F9.imprint","IMPRINT",FACE,{"disambiguationData":[TD([[makeQuery(id+"F9.imprint","IMPRINT",EDGE,{"derivedFrom":subQ1}),-1.0]])]});}
            extrude(context, id + "F11", {"entities" : qUnion([Q0, Q1]), "operationType" : NewBodyOperationType.REMOVE, "endBound" : BoundingType.SYMMETRIC, "oppositeDirection" : true, "depth" : 10 * mm});
        }
        {
            var Q0;
            Q0=makeQuery(id+"F1.opExtrude","SWEPT_EDGE",EDGE,{"disambiguationData":[OSD([sQuery(id+"F0.wireOp",EDGE,"E15.0"),sQuery(id+"F0.wireOp",EDGE,"E42.MirrorCS"),sQuery(id+"F0.wireOp",EDGE,"E49"),sQuery(id+"F0.wireOp",EDGE,"E53")])]});
            var Q1;
            Q1=makeQuery(id+"F1.opExtrude","SWEPT_EDGE",EDGE,{"disambiguationData":[OSD([sQuery(id+"F0.wireOp",EDGE,"E15.3"),sQuery(id+"F0.wireOp",EDGE,"E40.MirrorCS"),sQuery(id+"F0.wireOp",EDGE,"E50"),sQuery(id+"F0.wireOp",EDGE,"E53")])]});
            var Q2;
            Q2=makeQuery(id+"F1.opExtrude","SWEPT_EDGE",EDGE,{"disambiguationData":[OSD([sQuery(id+"F0.wireOp",EDGE,"E16.2"),sQuery(id+"F0.wireOp",EDGE,"E50"),sQuery(id+"F0.wireOp",EDGE,"E68")])]});
            var Q3;
            Q3=makeQuery(id+"F1.opExtrude","SWEPT_EDGE",EDGE,{"disambiguationData":[OSD([sQuery(id+"F0.wireOp",EDGE,"E16.1"),sQuery(id+"F0.wireOp",EDGE,"E49"),sQuery(id+"F0.wireOp",EDGE,"E67")])]});
            var Q4;
            Q4=makeQuery(id+"F1.opExtrude","CAP_EDGE",EDGE,{"disambiguationData":[OSD([sQuery(id+"F0.wireOp",EDGE,"E28.MirrorCS"),sQuery(id+"F0.wireOp",EDGE,"E44.MirrorCS")])],"isStart":false});
            var Q5;
            Q5=makeQuery(id+"F1.opExtrude","CAP_EDGE",EDGE,{"disambiguationData":[OSD([sQuery(id+"F0.wireOp",EDGE,"E28.MirrorCS"),sQuery(id+"F0.wireOp",EDGE,"E44.MirrorCS")])],"isStart":true});
            var Q6;
            Q6=makeQuery(id+"F1.opExtrude","CAP_EDGE",EDGE,{"disambiguationData":[OSD([sQuery(id+"F0.wireOp",EDGE,"E22.MirrorCS")])],"isStart":false});
            var Q7;
            Q7=makeQuery(id+"F1.opExtrude","CAP_EDGE",EDGE,{"disambiguationData":[OSD([sQuery(id+"F0.wireOp",EDGE,"E22.MirrorCS")])],"isStart":true});
            var Q8;
            Q8=makeQuery(id+"F1.opExtrude","CAP_EDGE",EDGE,{"disambiguationData":[OSD([sQuery(id+"F0.wireOp",EDGE,"E45.MirrorCS")])],"isStart":false});
            var Q9;
            Q9=makeQuery(id+"F1.opExtrude","CAP_EDGE",EDGE,{"disambiguationData":[OSD([sQuery(id+"F0.wireOp",EDGE,"E37.MirrorCS")])],"isStart":false});
            var Q10;
            Q10=makeQuery(id+"F1.opExtrude","CAP_EDGE",EDGE,{"disambiguationData":[OSD([sQuery(id+"F0.wireOp",EDGE,"E45.MirrorCS")])],"isStart":true});
            var Q11;
            Q11=makeQuery(id+"F1.opExtrude","CAP_EDGE",EDGE,{"disambiguationData":[OSD([sQuery(id+"F0.wireOp",EDGE,"E37.MirrorCS")])],"isStart":true});
            var Q12;
            Q12=makeQuery(id+"F1.opExtrude","CAP_EDGE",EDGE,{"disambiguationData":[OSD([sQuery(id+"F0.wireOp",EDGE,"E52")])],"isStart":false});
            var Q13;
            Q13=makeQuery(id+"F1.opExtrude","CAP_EDGE",EDGE,{"disambiguationData":[OSD([sQuery(id+"F0.wireOp",EDGE,"E52")])],"isStart":true});
            var Q14;
            Q14=makeQuery(id+"F1.opExtrude","CAP_EDGE",EDGE,{"disambiguationData":[OSD([sQuery(id+"F0.wireOp",EDGE,"E41.MirrorCS")])],"isStart":true});
            var Q15;
            Q15=makeQuery(id+"F1.opExtrude","CAP_EDGE",EDGE,{"disambiguationData":[OSD([sQuery(id+"F0.wireOp",EDGE,"E41.MirrorCS")])],"isStart":false});
            var Q16;
            Q16=makeQuery(id+"F1.opExtrude","SWEPT_EDGE",EDGE,{"disambiguationData":[OSD([sQuery(id+"F0.wireOp",EDGE,"E42.MirrorCS"),sQuery(id+"F0.wireOp",EDGE,"E44.MirrorCS")])]});
            var Q17;
            Q17=makeQuery(id+"F1.opExtrude","SWEPT_EDGE",EDGE,{"disambiguationData":[OSD([sQuery(id+"F0.wireOp",EDGE,"E40.MirrorCS"),sQuery(id+"F0.wireOp",EDGE,"E41.MirrorCS")])]});
            var Q18;
            Q18=makeQuery(id+"F1.opExtrude","SWEPT_EDGE",EDGE,{"disambiguationData":[OSD([sQuery(id+"F0.wireOp",EDGE,"E53"),sQuery(id+"F0.wireOp",EDGE,"E59")])]});
            var Q19;
            Q19=makeQuery(id+"F1.opExtrude","SWEPT_EDGE",EDGE,{"disambiguationData":[OSD([sQuery(id+"F0.wireOp",EDGE,"E53"),sQuery(id+"F0.wireOp",EDGE,"E60")])]});
            var Q20;
            Q20=makeQuery(id+"F1.opExtrude","SWEPT_EDGE",EDGE,{"disambiguationData":[OSD([sQuery(id+"F0.wireOp",EDGE,"E70"),sQuery(id+"F0.wireOp",EDGE,"E71")])]});
            var Q21;
            Q21=makeQuery(id+"F1.opExtrude","SWEPT_EDGE",EDGE,{"disambiguationData":[OSD([sQuery(id+"F0.wireOp",EDGE,"E73"),sQuery(id+"F0.wireOp",EDGE,"E74")])]});
            fillet(context, id + "F12", {"entities" : qUnion([Q0, Q1, Q2, Q3, Q4, Q5, Q6, Q7, Q8, Q9, Q10, Q11, Q12, Q13, Q14, Q15, Q16, Q17, Q18, Q19, Q20, Q21]), "radius" : 3 * mm, "tangentPropagation" : true, "allowEdgeOverflow" : false});
        }
        {
            var Q0;
            Q0=makeQuery(id+"F1.opExtrude","SWEPT_FACE",FACE,{"disambiguationData":[OSD([sQuery(id+"F0.wireOp",EDGE,"E29"),sQuery(id+"F0.wireOp",EDGE,"E30"),sQuery(id+"F0.wireOp",EDGE,"E31")])]});
            var sketch = newSketch(context, id + "F13", { "sketchPlane" : qUnion([Q0])});
            skLineSegment(sketch, "E87", {"start": v(0, 19) * mm, "end": v(0, 0) * mm, "construction": true});
            skLineSegment(sketch, "E88.0", {"start": v(-10.25, 19) * mm, "end": v(-10.25, 0) * mm});
            skLineSegment(sketch, "E89.0", {"start": v(10.25, 19) * mm, "end": v(10.25, 0) * mm});
            skPoint(sketch, "E90", {"position": v(0, 9.5) * mm});
            skSolve(sketch);
        }
        {
            var Q0;
            {var subQ0=sQuery(id+"F13.wireOp",EDGE,"E89.0");Q0=makeQuery(id+"F13.imprint","IMPRINT",FACE,{"disambiguationData":[TD([[makeQuery(id+"F13.imprint","IMPRINT",EDGE,{"derivedFrom":subQ0}),1.0]])]});}
            var Q1;
            {var subQ0=sQuery(id+"F13.wireOp",EDGE,"E88.0");Q1=makeQuery(id+"F13.imprint","IMPRINT",FACE,{"disambiguationData":[TD([[makeQuery(id+"F13.imprint","IMPRINT",EDGE,{"derivedFrom":subQ0}),-1.0]])]});}
            extrude(context, id + "F14", {"entities" : qUnion([Q0, Q1]), "operationType" : NewBodyOperationType.ADD, "depth" : 10 * mm});
        }
        {
            var Q0;
            Q0=makeQuery(id+"F1.opExtrude","SWEPT_FACE",FACE,{"disambiguationData":[OSD([sQuery(id+"F0.wireOp",EDGE,"E63"),sQuery(id+"F0.wireOp",EDGE,"E74")])]});
            var sketch = newSketch(context, id + "F15", { "sketchPlane" : qUnion([Q0])});
            skLineSegment(sketch, "E91", {"start": v(39.18, 0) * mm, "end": v(39.18, 19) * mm, "construction": true});
            skPoint(sketch, "E92", {"position": v(39.18, 5) * mm});
            skPoint(sketch, "E93", {"position": v(39.18, 14) * mm});
            skSolve(sketch);
        }
        {
            var Q0;
            Q0=sQuery(id+"F13.wireOp",VERTEX,"E90");
            var Q1;
            Q1=sQuery(id+"F15.wireOp",VERTEX,"E92");
            var Q2;
            Q2=sQuery(id+"F15.wireOp",VERTEX,"E93");
            var Q3;
            Q3=makeQuery(id+"F1.opExtrude","SWEPT_BODY",BODY,{"disambiguationData":[OSD([sQuery(id+"F0.wireOp",EDGE,"E15.0"),sQuery(id+"F0.wireOp",EDGE,"E15.1"),sQuery(id+"F0.wireOp",EDGE,"E15.2"),sQuery(id+"F0.wireOp",EDGE,"E15.3"),sQuery(id+"F0.wireOp",EDGE,"E16.0"),sQuery(id+"F0.wireOp",EDGE,"E16.1"),sQuery(id+"F0.wireOp",EDGE,"E16.2"),sQuery(id+"F0.wireOp",EDGE,"E16.3"),sQuery(id+"F0.wireOp",EDGE,"E20.MirrorCS"),sQuery(id+"F0.wireOp",EDGE,"E21.MirrorCS"),sQuery(id+"F0.wireOp",EDGE,"E22.MirrorCS"),sQuery(id+"F0.wireOp",EDGE,"E26.MirrorCS"),sQuery(id+"F0.wireOp",EDGE,"E27.MirrorCS"),sQuery(id+"F0.wireOp",EDGE,"E28.MirrorCS"),sQuery(id+"F0.wireOp",EDGE,"E29"),sQuery(id+"F0.wireOp",EDGE,"E30"),sQuery(id+"F0.wireOp",EDGE,"E31"),sQuery(id+"F0.wireOp",EDGE,"E32"),sQuery(id+"F0.wireOp",EDGE,"E33"),sQuery(id+"F0.wireOp",EDGE,"E34"),sQuery(id+"F0.wireOp",EDGE,"E35"),sQuery(id+"F0.wireOp",EDGE,"E36"),sQuery(id+"F0.wireOp",EDGE,"E37.MirrorCS"),sQuery(id+"F0.wireOp",EDGE,"E38.MirrorCS"),sQuery(id+"F0.wireOp",EDGE,"E39.MirrorCS"),sQuery(id+"F0.wireOp",EDGE,"E44.MirrorCS"),sQuery(id+"F0.wireOp",EDGE,"E45.MirrorCS"),sQuery(id+"F0.wireOp",EDGE,"E46.MirrorCS"),sQuery(id+"F0.wireOp",EDGE,"E47.MirrorCS"),sQuery(id+"F0.wireOp",EDGE,"E51"),sQuery(id+"F0.wireOp",EDGE,"E52"),sQuery(id+"F0.wireOp",EDGE,"E53"),sQuery(id+"F0.wireOp",EDGE,"E55"),sQuery(id+"F0.wireOp",EDGE,"E59"),sQuery(id+"F0.wireOp",EDGE,"E60"),sQuery(id+"F0.wireOp",EDGE,"E61"),sQuery(id+"F0.wireOp",EDGE,"E63"),sQuery(id+"F0.wireOp",EDGE,"E64"),sQuery(id+"F0.wireOp",EDGE,"E66"),sQuery(id+"F0.wireOp",EDGE,"E67"),sQuery(id+"F0.wireOp",EDGE,"E68"),sQuery(id+"F0.wireOp",EDGE,"E69"),sQuery(id+"F0.wireOp",EDGE,"E70"),sQuery(id+"F0.wireOp",EDGE,"E71"),sQuery(id+"F0.wireOp",EDGE,"E72"),sQuery(id+"F0.wireOp",EDGE,"E73"),sQuery(id+"F0.wireOp",EDGE,"E74")])]});
            hole(context, id + "F16", {"style" : HoleStyle.SIMPLE, "endStyle" : HoleEndStyle.BLIND, "holeDiameter" : 5 * mm, "holeDepth" : 15 * mm, "locations" : qUnion([Q0, Q1, Q2]), "scope" : qUnion([Q3])});
        }
    });
